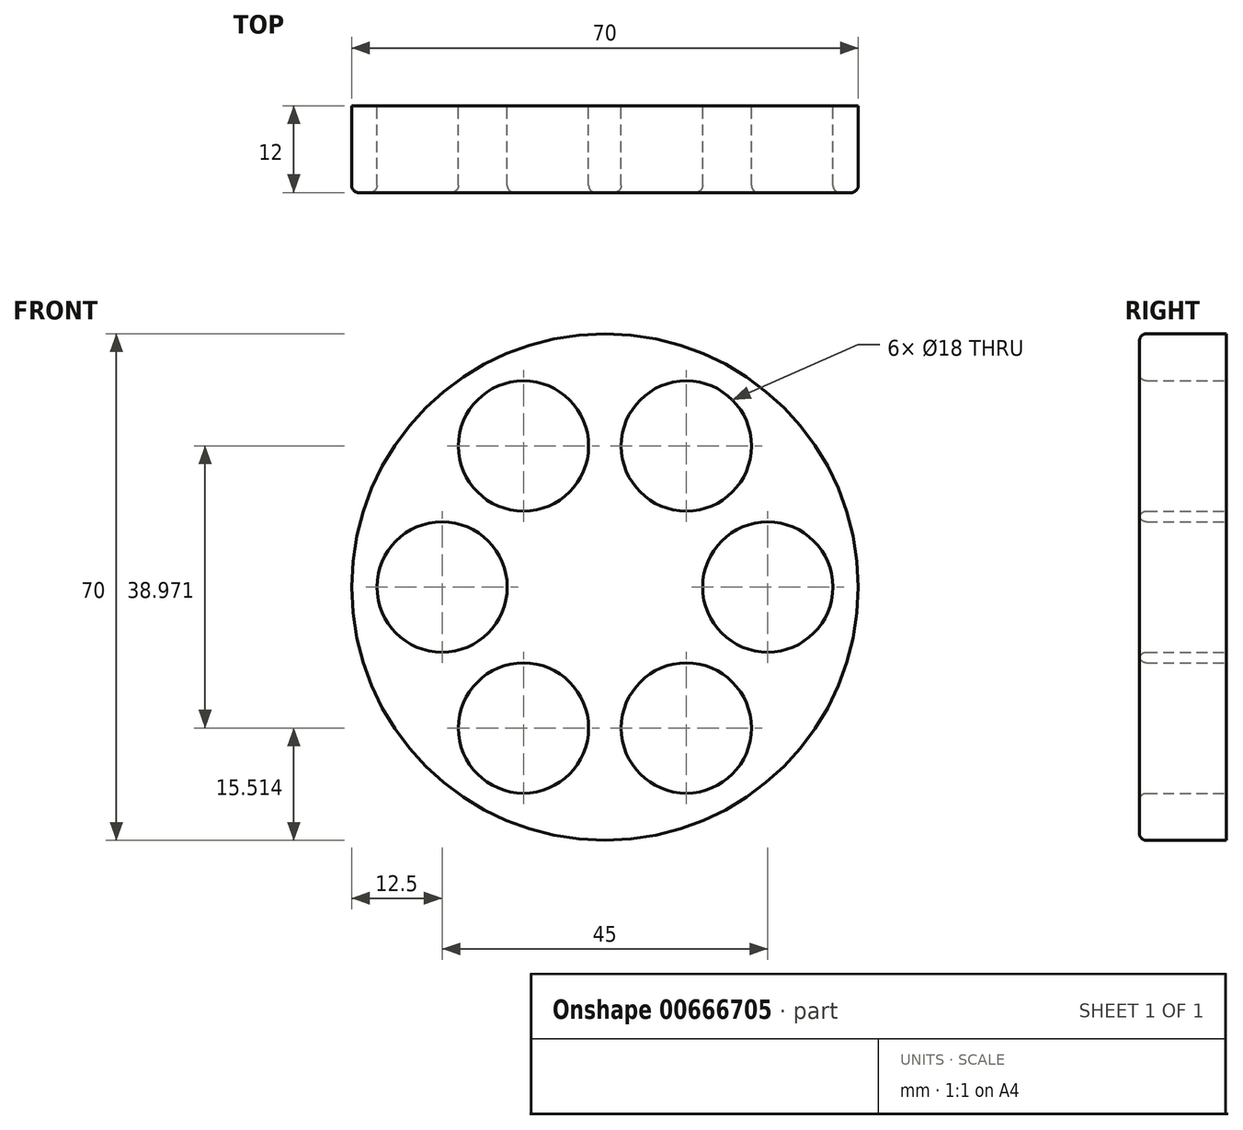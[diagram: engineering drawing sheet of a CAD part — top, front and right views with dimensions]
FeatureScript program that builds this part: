
annotation { "Feature Type Name" : "Feature", "Feature Type Description" : "" }
export const myFeature = defineFeature(function(context is Context, id is Id, definition is map)
    precondition{}
    {
        {
            var Q0;
            Q0=qCreatedBy(makeId("Front.planeOp"),FACE);
            var sketch = newSketch(context, id + "F0", { "sketchPlane" : qUnion([Q0])});
            skCircle(sketch, "E0", {"center": v(0, 0) * mm, "radius": 35 * mm});
            skCircle(sketch, "E1", {"center": v(-22.5, 0) * mm, "radius": 9 * mm});
            skCircle(sketch, "E2.1.0", {"center": v(-11.25, -19.49) * mm, "radius": 9 * mm});
            skCircle(sketch, "E2.2.0", {"center": v(11.25, -19.49) * mm, "radius": 9 * mm});
            skCircle(sketch, "E2.3.0", {"center": v(22.5, 0) * mm, "radius": 9 * mm});
            skCircle(sketch, "E2.4.0", {"center": v(11.25, 19.49) * mm, "radius": 9 * mm});
            skCircle(sketch, "E2.5.0", {"center": v(-11.25, 19.49) * mm, "radius": 9 * mm});
            skSolve(sketch);
        }
        {
            var Q0;
            Q0=makeQuery(id+"F0.imprint","IMPRINT",FACE,{"disambiguationData":[TD([[makeQuery(id+"F0.imprint","IMPRINT",EDGE,{"derivedFrom":sQuery(id+"F0.wireOp",EDGE,"E0")}),1.0]])]});
            extrude(context, id + "F1", {"entities" : qUnion([Q0]), "depth" : 12 * mm, "offsetDistance" : 25 * mm});
        }
        {
            var Q0;
            Q0=makeQuery(id+"F1.opExtrude","CAP_EDGE",EDGE,{"disambiguationData":[OSD([sQuery(id+"F0.wireOp",EDGE,"E0")])],"isStart":false});
            var Q1;
            Q1=makeQuery(id+"F1.opExtrude","CAP_EDGE",EDGE,{"disambiguationData":[OSD([sQuery(id+"F0.wireOp",EDGE,"E2.3.0")])],"isStart":false});
            var Q2;
            Q2=makeQuery(id+"F1.opExtrude","CAP_EDGE",EDGE,{"disambiguationData":[OSD([sQuery(id+"F0.wireOp",EDGE,"E2.4.0")])],"isStart":false});
            var Q3;
            Q3=makeQuery(id+"F1.opExtrude","CAP_EDGE",EDGE,{"disambiguationData":[OSD([sQuery(id+"F0.wireOp",EDGE,"E2.5.0")])],"isStart":false});
            var Q4;
            Q4=makeQuery(id+"F1.opExtrude","CAP_EDGE",EDGE,{"disambiguationData":[OSD([sQuery(id+"F0.wireOp",EDGE,"E1")])],"isStart":false});
            var Q5;
            Q5=makeQuery(id+"F1.opExtrude","CAP_EDGE",EDGE,{"disambiguationData":[OSD([sQuery(id+"F0.wireOp",EDGE,"E2.1.0")])],"isStart":false});
            var Q6;
            Q6=makeQuery(id+"F1.opExtrude","CAP_EDGE",EDGE,{"disambiguationData":[OSD([sQuery(id+"F0.wireOp",EDGE,"E2.2.0")])],"isStart":false});
            fillet(context, id + "F2", {"entities" : qUnion([Q0, Q1, Q2, Q3, Q4, Q5, Q6]), "radius" : 1 * mm, "tangentPropagation" : true, "allowEdgeOverflow" : false});
        }
    });
